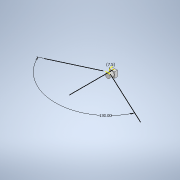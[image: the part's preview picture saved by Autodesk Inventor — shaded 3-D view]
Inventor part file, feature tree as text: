
AUTODESK INVENTOR PART (.ipt)
format: ipt  version: 2020 (Build 240168000, 168)  size: 131,072 bytes
history: native  units: in
note: dims shown in document units (in); Inventor stores cm internally (conversion verified against a paired STEP export)
features: sketch x5, extrude x3, projected_geometry x1
ambient origin geometry x8: Origin, YZ Plane, XZ Plane, XY Plane, X Axis, Y Axis, Z Axis, Center Point
bodies: Solid1 (feature_tree)
feature tree (9):
  extrude  "Extrusion1"  Depth=0.5689in
  sketch  "Sketch6"  dims[d2=0.2953in d3=0.0in d14=0.4724in]
  sketch  "Sketch7"  dims[d15=0.2953in d16=0.4134in d17=0.0in]
  extrude  "Extrusion4"  Depth=0.2953in
  extrude  "Extrusion5"  Depth=0.4134in TaperAngle=0.0deg
  sketch  "Sketch10"  dims[d19=0.0787in d20=0.7087in d21=0.0in d22=0.8933in]
  sketch  "Sketch1"  dims[d0=0.5689in d1=0.5689in]
  projected_geometry  "Projected Loop4"
  sketch  "Sketch8"  dims[d18=0.1969in]
